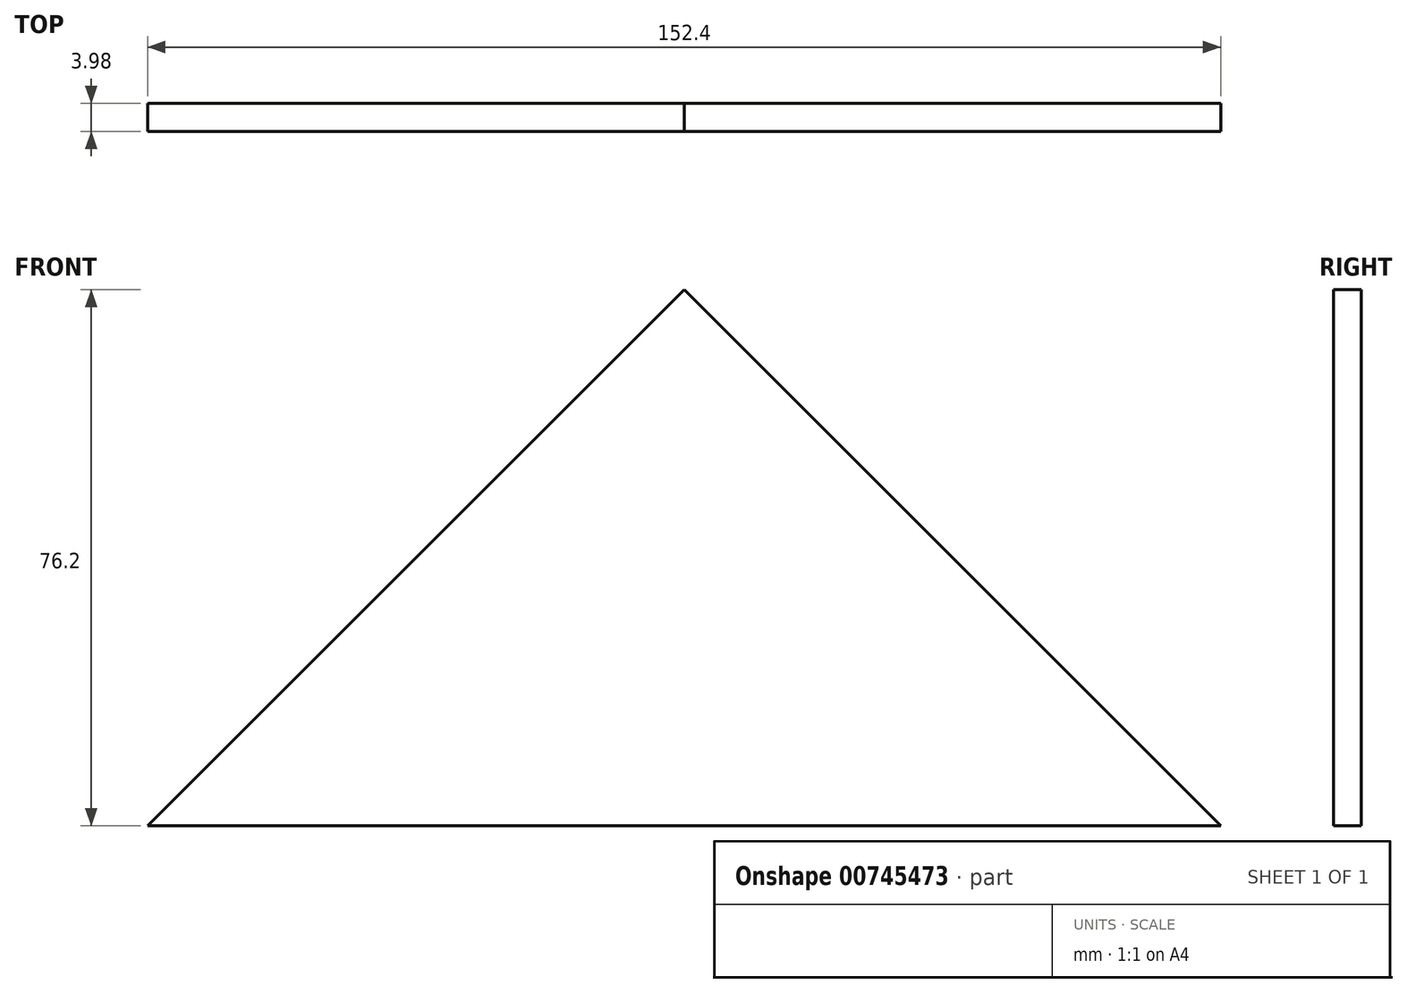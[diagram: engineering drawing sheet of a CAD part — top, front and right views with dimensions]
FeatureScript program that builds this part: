
annotation { "Feature Type Name" : "Feature", "Feature Type Description" : "" }
export const myFeature = defineFeature(function(context is Context, id is Id, definition is map)
    precondition{}
    {
        {
            var Q0;
            Q0=qCreatedBy(makeId("Front.planeOp"),FACE);
            var sketch = newSketch(context, id + "F0", { "sketchPlane" : qUnion([Q0])});
            skLineSegment(sketch, "E0", {"start": v(0, 0) * mm, "end": v(-76.2, 0) * mm});
            skLineSegment(sketch, "E1", {"start": v(-76.2, 0) * mm, "end": v(0, 76.2) * mm});
            skLineSegment(sketch, "E2", {"start": v(0, 76.2) * mm, "end": v(76.2, 0) * mm});
            skLineSegment(sketch, "E3", {"start": v(76.2, 0) * mm, "end": v(0, 0) * mm});
            skSolve(sketch);
        }
        {
            var Q0;
            Q0=makeQuery(id+"F0.imprint","IMPRINT",FACE,{"disambiguationData":[TD([[makeQuery(id+"F0.imprint","IMPRINT",EDGE,{"derivedFrom":sQuery(id+"F0.wireOp",EDGE,"E0")}),-1.0]])]});
            extrude(context, id + "F1", {"entities" : qUnion([Q0]), "depth" : 3.98 * mm, "offsetDistance" : 25.4 * mm});
        }
    });
